# Revit family: PFRD-ACPMK
name_source: partatom
category: Lighting Fixtures
units: mm (PartAtom-declared; Revit-internal decimal feet)

## family parameters
Cut with Voids When Loaded = Yes
Host = Face
Light Source = Yes
Maintain Annotation Orientation = No
Part Type = Normal
Room Calculation Point = No
Round Connector Dimension = Use Diameter
Shared = No

## types (5) — shared parameters
CRI = 90
Color Filter = 16777215
Default Elevation = 0' - 0"
Dimming Lamp Color Temperature Shift = <None>
Input Voltage = 120-277V
Lamp = LED
Load Classification = Lighting
Manufacturer = Above All Lighting
Note = Max. Aircraft Cable and Wire Cord Length: 59" (1500mm).
Power Factor = 0.9
Suspended = 3' - 0"
Tilt Angle = 90.00°
URL = https://www.abovealllighting.com

## per-type parameters (varying)
| type | A | Lens | Model | Photometric Web File | R | Wattage Comments | r |
| PFRD16-20W-3000K-ACPMK | 0' - 5" | 0' - 7 19/32" | PFRD16-20-30901-ACPMK-WH | PFRD16-20W-3000K.IES | 0' - 7 27/32" | 20W | 0' - 2 5/8" |
| PFRD19-25W-3000K-ACPMK | 0' - 5" | 0' - 9 3/16" | PFRD19-25-30901-ACPMK-WH | PFRD19-25W-3000K.IES | 0' - 9 7/16" | 25W | 0' - 3 5/32" |
| PFRD35-90W-3000K-ACPMK | 0' - 5" | 1' - 5 3/8" | PFRD35-90-30901-ACPMK-WH | PFRD35-90W-3000K.IES | 1' - 5 5/8" | 90W | 0' - 5 7/8" |
| PFRD47-180W-3000K-ACPMK | 0' - 6 29/32" | 1' - 11 11/32" | PFRD47-180-30901-ACPMK-WH | PFRD47-180W-3000K.IES | 1' - 11 19/32" | 180W | 0' - 7 7/8" |
| PFRD59-220W-3000K-ACPMK | 0' - 8 27/32" | 2' - 5 1/4" | PFRD59-220-30901-ACPMK-WH | PFRD59-220W-3000K.IES | 2' - 5 1/2" | 220W | 0' - 9 27/32" |

## geometry (parser evidence)
native form markers: Sweep x2
no freeform markers — native parametric forms only
